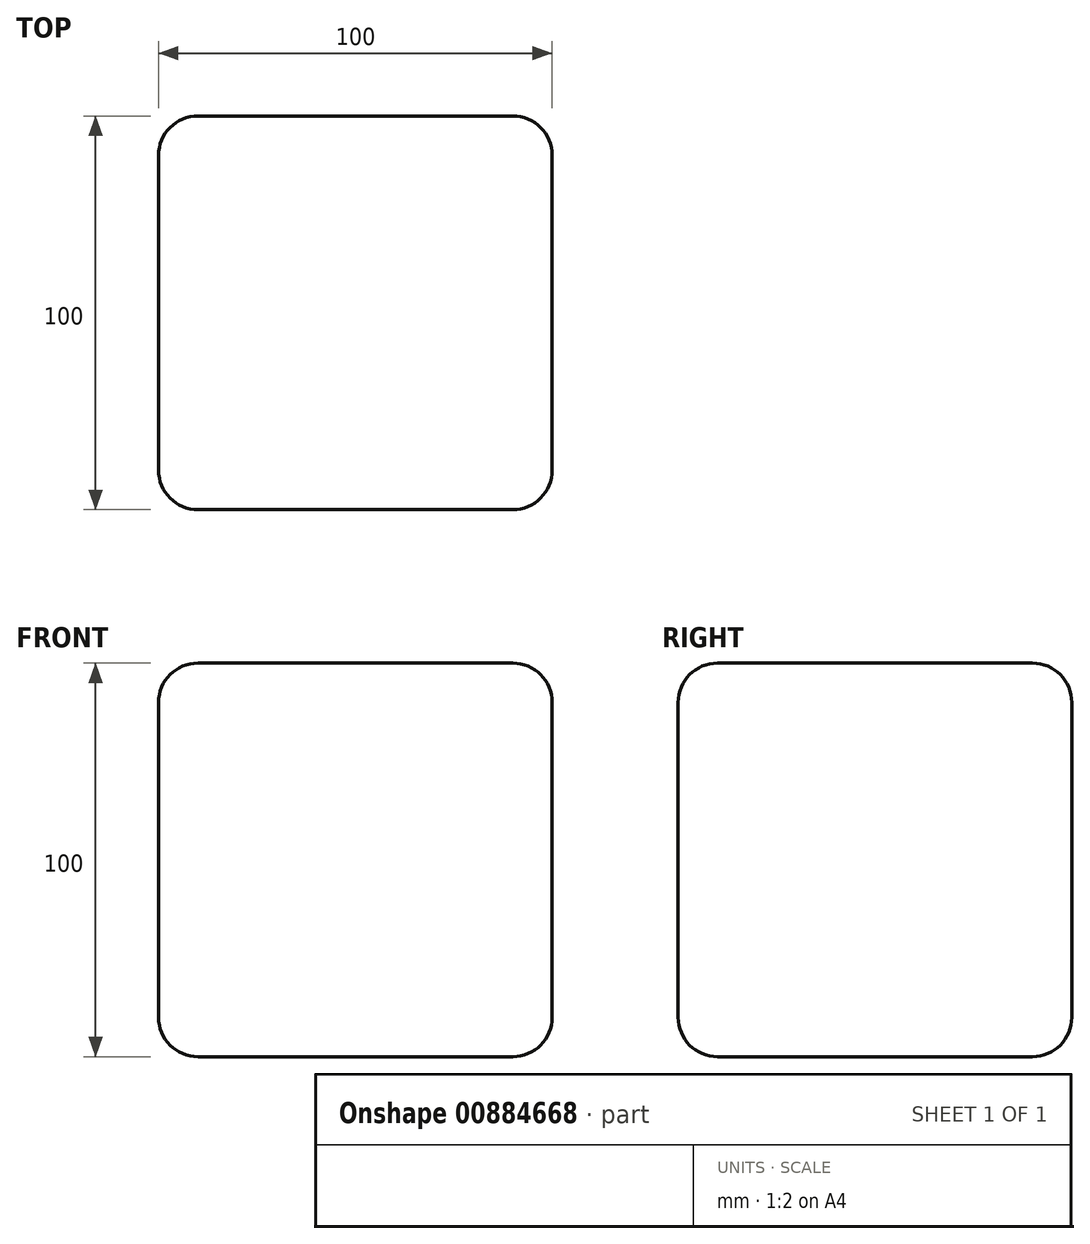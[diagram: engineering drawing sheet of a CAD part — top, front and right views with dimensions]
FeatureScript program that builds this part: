
annotation { "Feature Type Name" : "Feature", "Feature Type Description" : "" }
export const myFeature = defineFeature(function(context is Context, id is Id, definition is map)
    precondition{}
    {
        {
            var Q0;
            Q0=qCreatedBy(makeId("Top.planeOp"),FACE);
            var sketch = newSketch(context, id + "F0", { "sketchPlane" : qUnion([Q0])});
            skLineSegment(sketch, "E0.bottom", {"start": v(56.36, 50) * mm, "end": v(-43.64, 50) * mm});
            skLineSegment(sketch, "E0.top", {"start": v(56.36, -50) * mm, "end": v(-43.64, -50) * mm});
            skLineSegment(sketch, "E0.left", {"start": v(56.36, 50) * mm, "end": v(56.36, -50) * mm});
            skLineSegment(sketch, "E0.right", {"start": v(-43.64, 50) * mm, "end": v(-43.64, -50) * mm});
            skPoint(sketch, "E0.middle", {"position": v(6.36, 0) * mm});
            skSolve(sketch);
        }
        {
            var Q0;
            Q0 = qSketchRegion(id + "F0", true);
            extrude(context, id + "F1", {"entities" : qUnion([Q0]), "depth" : 100 * mm, "offsetDistance" : 25 * mm});
        }
        {
            var Q0;
            Q0=makeQuery(id+"F1.opExtrude","CAP_EDGE",EDGE,{"disambiguationData":[OSD([sQuery(id+"F0.wireOp",EDGE,"E0.top")])],"isStart":false});
            var Q1;
            Q1=makeQuery(id+"F1.opExtrude","CAP_EDGE",EDGE,{"disambiguationData":[OSD([sQuery(id+"F0.wireOp",EDGE,"E0.right")])],"isStart":false});
            var Q2;
            Q2=makeQuery(id+"F1.opExtrude","CAP_EDGE",EDGE,{"disambiguationData":[OSD([sQuery(id+"F0.wireOp",EDGE,"E0.left")])],"isStart":false});
            var Q3;
            Q3=makeQuery(id+"F1.opExtrude","CAP_EDGE",EDGE,{"disambiguationData":[OSD([sQuery(id+"F0.wireOp",EDGE,"E0.bottom")])],"isStart":false});
            var Q4;
            Q4=makeQuery(id+"F1.opExtrude","SWEPT_EDGE",EDGE,{"disambiguationData":[OSD([sQuery(id+"F0.wireOp",EDGE,"E0.top"),sQuery(id+"F0.wireOp",EDGE,"E0.left")])]});
            var Q5;
            Q5=makeQuery(id+"F1.opExtrude","SWEPT_EDGE",EDGE,{"disambiguationData":[OSD([sQuery(id+"F0.wireOp",EDGE,"E0.top"),sQuery(id+"F0.wireOp",EDGE,"E0.right")])]});
            var Q6;
            Q6=makeQuery(id+"F1.opExtrude","SWEPT_EDGE",EDGE,{"disambiguationData":[OSD([sQuery(id+"F0.wireOp",EDGE,"E0.bottom"),sQuery(id+"F0.wireOp",EDGE,"E0.right")])]});
            var Q7;
            Q7=makeQuery(id+"F1.opExtrude","SWEPT_EDGE",EDGE,{"disambiguationData":[OSD([sQuery(id+"F0.wireOp",EDGE,"E0.bottom"),sQuery(id+"F0.wireOp",EDGE,"E0.left")])]});
            var Q8;
            Q8=makeQuery(id+"F1.opExtrude","CAP_EDGE",EDGE,{"disambiguationData":[OSD([sQuery(id+"F0.wireOp",EDGE,"E0.left")])],"isStart":true});
            var Q9;
            Q9=makeQuery(id+"F1.opExtrude","CAP_EDGE",EDGE,{"disambiguationData":[OSD([sQuery(id+"F0.wireOp",EDGE,"E0.top")])],"isStart":true});
            var Q10;
            Q10=makeQuery(id+"F1.opExtrude","CAP_EDGE",EDGE,{"disambiguationData":[OSD([sQuery(id+"F0.wireOp",EDGE,"E0.bottom")])],"isStart":true});
            var Q11;
            Q11=makeQuery(id+"F1.opExtrude","CAP_EDGE",EDGE,{"disambiguationData":[OSD([sQuery(id+"F0.wireOp",EDGE,"E0.right")])],"isStart":true});
            fillet(context, id + "F2", {"entities" : qUnion([Q0, Q1, Q2, Q3, Q4, Q5, Q6, Q7, Q8, Q9, Q10, Q11]), "radius" : 10 * mm, "tangentPropagation" : true, "allowEdgeOverflow" : false});
        }
    });
